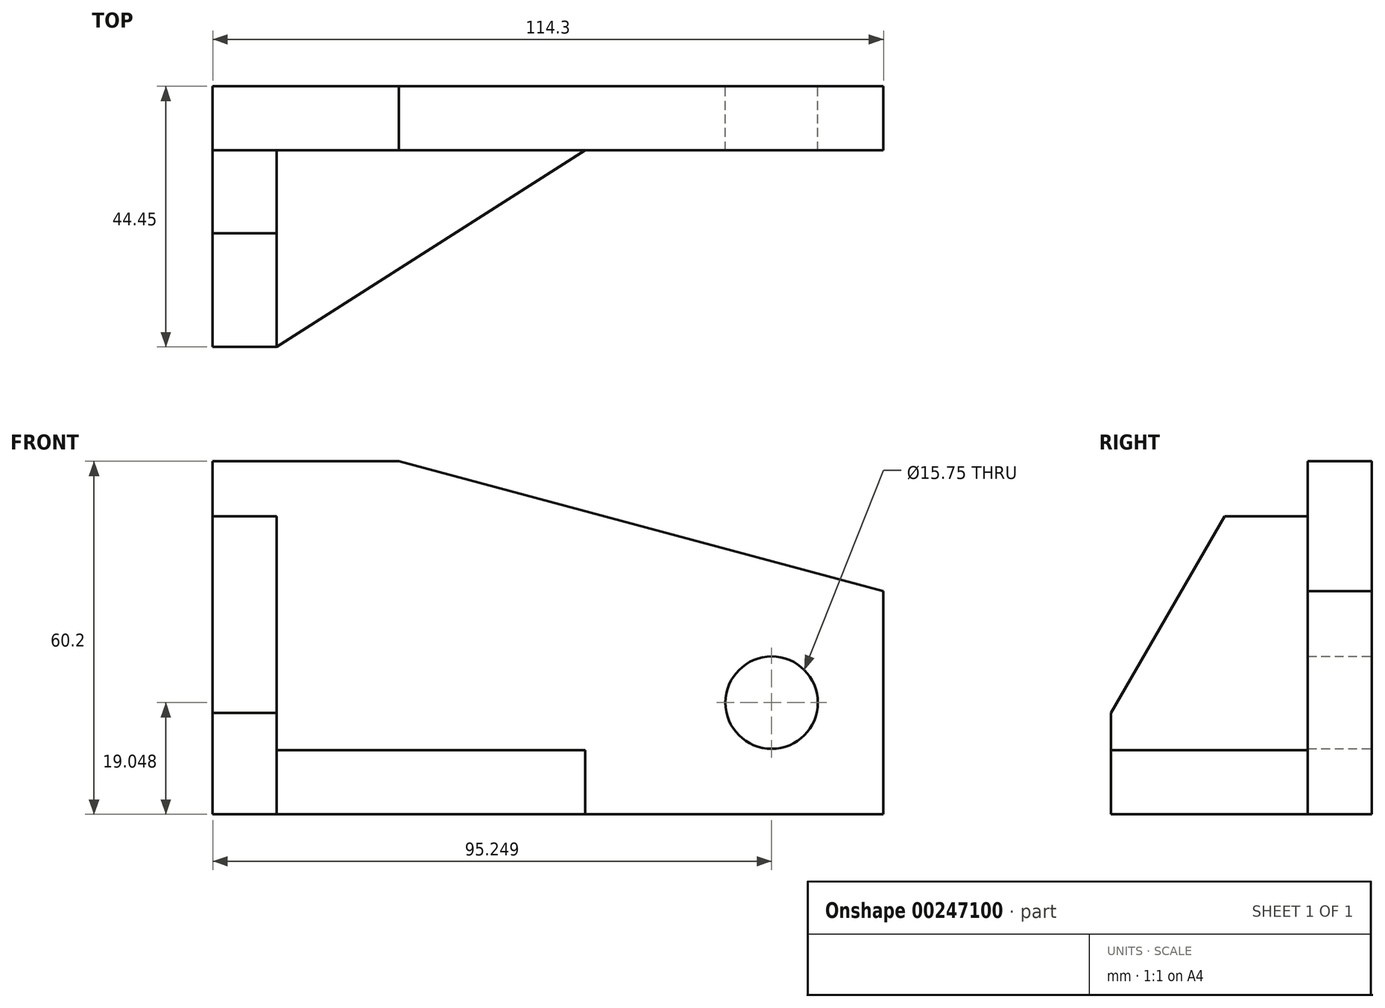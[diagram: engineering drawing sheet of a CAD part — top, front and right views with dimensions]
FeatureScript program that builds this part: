
annotation { "Feature Type Name" : "Feature", "Feature Type Description" : "" }
export const myFeature = defineFeature(function(context is Context, id is Id, definition is map)
    precondition{}
    {
        {
            var Q0;
            Q0=qCreatedBy(makeId("Front.planeOp"),FACE);
            var sketch = newSketch(context, id + "F0", { "sketchPlane" : qUnion([Q0])});
            skLineSegment(sketch, "E0.bottom", {"start": v(-55.28, 38.8) * mm, "end": v(-23.53, 38.8) * mm});
            skLineSegment(sketch, "E0.top", {"start": v(-55.28, -21.4) * mm, "end": v(59.02, -21.4) * mm});
            skLineSegment(sketch, "E0.right", {"start": v(59.02, 16.68) * mm, "end": v(59.02, -21.4) * mm});
            skPoint(sketch, "E1", {"position": v(-23.53, 38.8) * mm});
            skLineSegment(sketch, "E2", {"start": v(-23.53, 38.8) * mm, "end": v(59.02, 16.68) * mm});
            skCircle(sketch, "E3", {"center": v(39.97, -2.35) * mm, "radius": 7.87 * mm});
            skPoint(sketch, "E4", {"position": v(8.22, -21.4) * mm});
            skLineSegment(sketch, "E5.bottom", {"start": v(-55.28, 29.4) * mm, "end": v(-44.36, 29.4) * mm});
            skLineSegment(sketch, "E5.right", {"start": v(-44.36, 29.4) * mm, "end": v(-44.36, -21.4) * mm});
            skLineSegment(sketch, "E6.top", {"start": v(8.22, -10.48) * mm, "end": v(-44.36, -10.48) * mm});
            skLineSegment(sketch, "E6.left", {"start": v(8.22, -21.4) * mm, "end": v(8.22, -10.48) * mm});
            skLineSegment(sketch, "E6.right", {"start": v(-55.28, -21.4) * mm, "end": v(-55.28, 38.8) * mm});
            skLineSegment(sketch, "E7", {"start": v(-55.28, 0.7) * mm, "end": v(-44.36, 0.7) * mm});
            skSolve(sketch);
        }
        {
            var Q0;
            Q0=makeQuery(id+"F0.imprint","IMPRINT",FACE,{"disambiguationData":[TD([[makeQuery(id+"F0.imprint","IMPRINT",EDGE,{"derivedFrom":sQuery(id+"F0.wireOp",EDGE,"E0.bottom")}),-1.0]])]});
            var Q1;
            {var subQ3=sQuery(id+"F0.wireOp",EDGE,"E7");Q1=makeQuery(id+"F0.imprint","IMPRINT",FACE,{"disambiguationData":[TD([[makeQuery(id+"F0.imprint","IMPRINT",EDGE,{"derivedFrom":subQ3}),-1.0]])]});}
            var Q2;
            {var subQ4=sQuery(id+"F0.wireOp",EDGE,"E6.top");Q2=makeQuery(id+"F0.imprint","IMPRINT",FACE,{"disambiguationData":[TD([[makeQuery(id+"F0.imprint","IMPRINT",EDGE,{"derivedFrom":subQ4}),1.0]])]});}
            var Q3;
            {var subQ0=sQuery(id+"F0.wireOp",EDGE,"E5.bottom");Q3=makeQuery(id+"F0.imprint","IMPRINT",FACE,{"disambiguationData":[TD([[makeQuery(id+"F0.imprint","IMPRINT",EDGE,{"derivedFrom":subQ0}),-1.0]])]});}
            extrude(context, id + "F1", {"entities" : qUnion([Q0, Q1, Q2, Q3]), "depth" : 10.92 * mm});
        }
        {
            var Q0;
            {var subQ3=sQuery(id+"F0.wireOp",EDGE,"E7");Q0=makeQuery(id+"F0.imprint","IMPRINT",FACE,{"disambiguationData":[TD([[makeQuery(id+"F0.imprint","IMPRINT",EDGE,{"derivedFrom":subQ3}),-1.0]])]});}
            var Q1;
            {var subQ0=sQuery(id+"F0.wireOp",EDGE,"E5.bottom");Q1=makeQuery(id+"F0.imprint","IMPRINT",FACE,{"disambiguationData":[TD([[makeQuery(id+"F0.imprint","IMPRINT",EDGE,{"derivedFrom":subQ0}),-1.0]])]});}
            var Q2;
            {var subQ4=sQuery(id+"F0.wireOp",EDGE,"E6.top");Q2=makeQuery(id+"F0.imprint","IMPRINT",FACE,{"disambiguationData":[TD([[makeQuery(id+"F0.imprint","IMPRINT",EDGE,{"derivedFrom":subQ4}),1.0]])]});}
            extrude(context, id + "F2", {"entities" : qUnion([Q0, Q1, Q2]), "operationType" : NewBodyOperationType.ADD, "depth" : 44.45 * mm});
        }
        {
            var Q0;
            Q0=makeQuery(id+"F2.opExtrude","SWEPT_FACE",FACE,{"disambiguationData":[OSD([sQuery(id+"F0.wireOp",EDGE,"E6.top")])]});
            var sketch = newSketch(context, id + "F3", { "sketchPlane" : qUnion([Q0])});
            skLineSegment(sketch, "E8", {"start": v(-44.36, -44.45) * mm, "end": v(8.22, -10.92) * mm});
            skSolve(sketch);
        }
        {
            var Q0;
            Q0=makeQuery(id+"F3.imprint","IMPRINT",FACE,{"disambiguationData":[TD([[makeQuery(id+"F3.imprint","IMPRINT",EDGE,{"derivedFrom":sQuery(id+"F3.wireOp",EDGE,"E8")}),-1.0]])]});
            extrude(context, id + "F4", {"entities" : qUnion([Q0]), "operationType" : NewBodyOperationType.REMOVE, "oppositeDirection" : true, "depth" : 25.4 * mm});
        }
        {
            var Q0;
            Q0=makeQuery(id+"F2.opExtrude","SWEPT_FACE",FACE,{"disambiguationData":[OSD([sQuery(id+"F0.wireOp",EDGE,"E5.right")])]});
            var sketch = newSketch(context, id + "F5", { "sketchPlane" : qUnion([Q0])});
            skLineSegment(sketch, "E9", {"start": v(-44.45, -4.13) * mm, "end": v(-25.1, 29.4) * mm});
            skSolve(sketch);
        }
        {
            var Q0;
            {var subQ0=sQuery(id+"F5.wireOp",EDGE,"E9");Q0=makeQuery(id+"F5.imprint","IMPRINT",FACE,{"disambiguationData":[TD([[makeQuery(id+"F5.imprint","IMPRINT",EDGE,{"derivedFrom":subQ0}),1.0]])]});}
            extrude(context, id + "F6", {"entities" : qUnion([Q0]), "operationType" : NewBodyOperationType.REMOVE, "oppositeDirection" : true, "depth" : 25.4 * mm});
        }
    });
